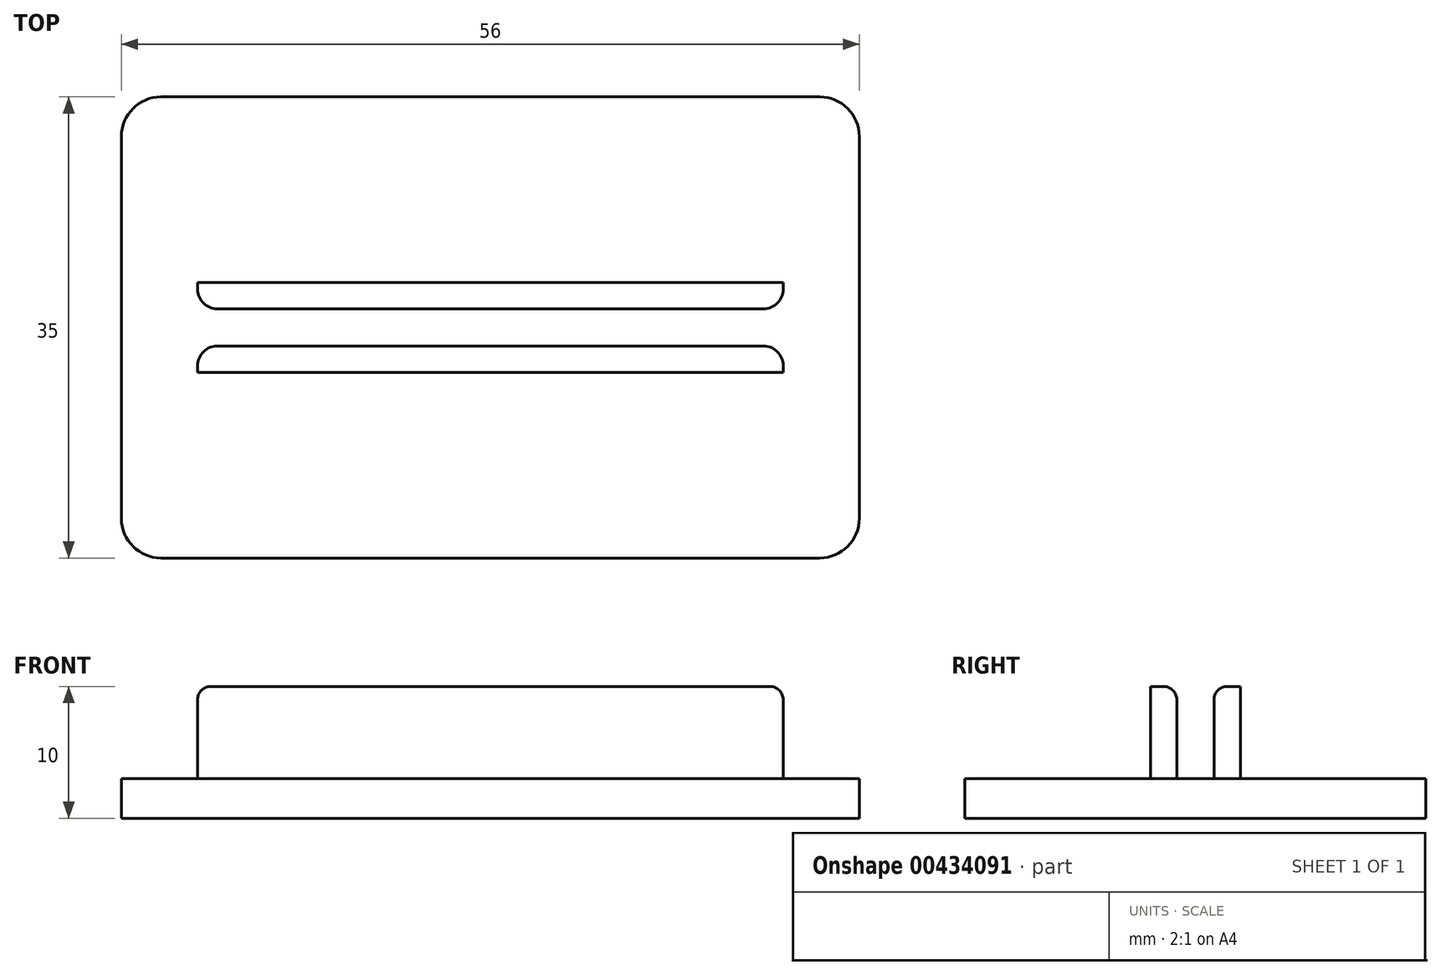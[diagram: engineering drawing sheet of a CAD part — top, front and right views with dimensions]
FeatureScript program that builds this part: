
annotation { "Feature Type Name" : "Feature", "Feature Type Description" : "" }
export const myFeature = defineFeature(function(context is Context, id is Id, definition is map)
    precondition{}
    {
        {
            var Q0;
            Q0=qCreatedBy(makeId("Top.planeOp"),FACE);
            var sketch = newSketch(context, id + "F0", { "sketchPlane" : qUnion([Q0])});
            skLineSegment(sketch, "E0.bottom", {"start": v(-65.71, 51.56) * mm, "end": v(-9.71, 51.56) * mm});
            skLineSegment(sketch, "E0.top", {"start": v(-65.71, 16.56) * mm, "end": v(-9.71, 16.56) * mm});
            skLineSegment(sketch, "E0.left", {"start": v(-65.71, 51.56) * mm, "end": v(-65.71, 16.56) * mm});
            skLineSegment(sketch, "E0.right", {"start": v(-9.71, 51.56) * mm, "end": v(-9.71, 16.56) * mm});
            skLineSegment(sketch, "E1", {"start": v(-81.04, 34.06) * mm, "end": v(-59.94, 34.06) * mm, "construction": true});
            skPoint(sketch, "E1.startSnap0", {"position": v(-65.71, 34.06) * mm});
            skLineSegment(sketch, "E2", {"start": v(-37.71, 62.88) * mm, "end": v(-37.71, 8.4) * mm, "construction": true});
            skPoint(sketch, "E2.startSnap0", {"position": v(-37.71, 51.56) * mm});
            skLineSegment(sketch, "E3.0", {"start": v(-81.04, 32.65) * mm, "end": v(7.2, 32.65) * mm, "construction": true});
            skLineSegment(sketch, "E4.0", {"start": v(-81.04, 35.47) * mm, "end": v(7.2, 35.47) * mm, "construction": true});
            skLineSegment(sketch, "E5", {"start": v(-59.94, 41.1) * mm, "end": v(-59.94, 35.47) * mm, "construction": true});
            skLineSegment(sketch, "E6.MirrorCS", {"start": v(-15.49, 41.1) * mm, "end": v(-15.49, 25.23) * mm, "construction": true});
            skLineSegment(sketch, "E7.bottom", {"start": v(-59.94, 35.47) * mm, "end": v(-15.49, 35.47) * mm, "construction": true});
            skLineSegment(sketch, "E7.top", {"start": v(-59.94, 37.47) * mm, "end": v(-15.49, 37.47) * mm, "construction": true});
            skLineSegment(sketch, "E7.left", {"start": v(-59.94, 35.47) * mm, "end": v(-59.94, 37.47) * mm, "construction": true});
            skLineSegment(sketch, "E7.right", {"start": v(-15.49, 35.47) * mm, "end": v(-15.49, 37.47) * mm, "construction": true});
            skLineSegment(sketch, "E8.top", {"start": v(-59.94, 32.65) * mm, "end": v(-15.49, 32.65) * mm});
            skLineSegment(sketch, "E8.right", {"start": v(-15.49, 34.06) * mm, "end": v(-15.49, 32.65) * mm});
            skLineSegment(sketch, "E9.bottom", {"start": v(-59.94, 37.47) * mm, "end": v(-15.49, 37.47) * mm});
            skLineSegment(sketch, "E9.top", {"start": v(-59.94, 35.47) * mm, "end": v(-15.49, 35.47) * mm});
            skLineSegment(sketch, "E9.left", {"start": v(-59.94, 37.47) * mm, "end": v(-59.94, 35.47) * mm});
            skLineSegment(sketch, "E9.right", {"start": v(-15.49, 37.47) * mm, "end": v(-15.49, 35.47) * mm});
            skLineSegment(sketch, "E10.trimOffspring", {"start": v(-15.49, 34.06) * mm, "end": v(7.2, 34.06) * mm, "construction": true});
            skLineSegment(sketch, "E11.trimOffspring", {"start": v(-59.94, 32.65) * mm, "end": v(-59.94, 25.23) * mm, "construction": true});
            skLineSegment(sketch, "E12.top", {"start": v(-59.94, 30.65) * mm, "end": v(-15.49, 30.65) * mm});
            skLineSegment(sketch, "E12.left", {"start": v(-59.94, 32.65) * mm, "end": v(-59.94, 30.65) * mm});
            skLineSegment(sketch, "E12.right", {"start": v(-15.49, 32.65) * mm, "end": v(-15.49, 30.65) * mm});
            skLineSegment(sketch, "E13", {"start": v(-59.94, 34.06) * mm, "end": v(-15.49, 34.06) * mm, "construction": true});
            skSolve(sketch);
        }
        {
            var Q0;
            Q0=makeQuery(id+"F0.imprint","IMPRINT",FACE,{"disambiguationData":[TD([[makeQuery(id+"F0.imprint","IMPRINT",EDGE,{"derivedFrom":sQuery(id+"F0.wireOp",EDGE,"E0.bottom")}),-1.0]])]});
            extrude(context, id + "F1", {"entities" : qUnion([Q0]), "depth" : 3 * mm, "offsetDistance" : 25 * mm});
        }
        {
            var Q0;
            Q0=makeQuery(id+"F0.imprint","IMPRINT",FACE,{"disambiguationData":[TD([[makeQuery(id+"F0.imprint","IMPRINT",EDGE,{"derivedFrom":sQuery(id+"F0.wireOp",EDGE,"E8.top")}),-1.0]])]});
            var Q1;
            Q1=makeQuery(id+"F0.imprint","IMPRINT",FACE,{"disambiguationData":[TD([[makeQuery(id+"F0.imprint","IMPRINT",EDGE,{"derivedFrom":sQuery(id+"F0.wireOp",EDGE,"E9.bottom")}),-1.0]])]});
            extrude(context, id + "F2", {"entities" : qUnion([Q0, Q1]), "operationType" : NewBodyOperationType.ADD, "depth" : 10 * mm, "offsetDistance" : 25 * mm});
        }
        {
            var Q0;
            Q0=makeQuery(id+"F2.opExtrude","SWEPT_EDGE",EDGE,{"disambiguationData":[OSD([sQuery(id+"F0.wireOp",EDGE,"E9.top"),sQuery(id+"F0.wireOp",EDGE,"E9.left")])]});
            var Q1;
            Q1=makeQuery(id+"F2.opExtrude","SWEPT_EDGE",EDGE,{"disambiguationData":[OSD([sQuery(id+"F0.wireOp",EDGE,"E8.top"),sQuery(id+"F0.wireOp",EDGE,"E12.left")])]});
            var Q2;
            Q2=makeQuery(id+"F2.opExtrude","SWEPT_EDGE",EDGE,{"disambiguationData":[OSD([sQuery(id+"F0.wireOp",EDGE,"E9.top"),sQuery(id+"F0.wireOp",EDGE,"E9.right")])]});
            var Q3;
            Q3=makeQuery(id+"F2.opExtrude","SWEPT_EDGE",EDGE,{"disambiguationData":[OSD([sQuery(id+"F0.wireOp",EDGE,"E8.top"),sQuery(id+"F0.wireOp",EDGE,"E12.right")])]});
            fillet(context, id + "F3", {"entities" : qUnion([Q0, Q1, Q2, Q3]), "radius" : 1.5 * mm, "tangentPropagation" : true, "allowEdgeOverflow" : false});
        }
        {
            var Q0;
            Q0=makeQuery(id+"F2.opExtrude","CAP_EDGE",EDGE,{"disambiguationData":[OSD([sQuery(id+"F0.wireOp",EDGE,"E9.top")])],"isStart":false});
            var Q1;
            Q1=makeQuery(id+"F2.opExtrude","CAP_EDGE",EDGE,{"disambiguationData":[OSD([sQuery(id+"F0.wireOp",EDGE,"E8.top")])],"isStart":false});
            fillet(context, id + "F4", {"entities" : qUnion([Q0, Q1]), "radius" : 1 * mm, "tangentPropagation" : true, "allowEdgeOverflow" : false});
        }
        {
            var Q0;
            Q0=makeQuery(id+"F1.opExtrude","SWEPT_EDGE",EDGE,{"disambiguationData":[OSD([sQuery(id+"F0.wireOp",EDGE,"E0.bottom"),sQuery(id+"F0.wireOp",EDGE,"E0.right")])]});
            var Q1;
            Q1=makeQuery(id+"F1.opExtrude","SWEPT_EDGE",EDGE,{"disambiguationData":[OSD([sQuery(id+"F0.wireOp",EDGE,"E0.top"),sQuery(id+"F0.wireOp",EDGE,"E0.left")])]});
            var Q2;
            Q2=makeQuery(id+"F1.opExtrude","SWEPT_EDGE",EDGE,{"disambiguationData":[OSD([sQuery(id+"F0.wireOp",EDGE,"E0.bottom"),sQuery(id+"F0.wireOp",EDGE,"E0.left")])]});
            var Q3;
            Q3=makeQuery(id+"F1.opExtrude","SWEPT_EDGE",EDGE,{"disambiguationData":[OSD([sQuery(id+"F0.wireOp",EDGE,"E0.top"),sQuery(id+"F0.wireOp",EDGE,"E0.right")])]});
            fillet(context, id + "F5", {"entities" : qUnion([Q0, Q1, Q2, Q3]), "radius" : 3 * mm, "tangentPropagation" : true, "allowEdgeOverflow" : false});
        }
    });
